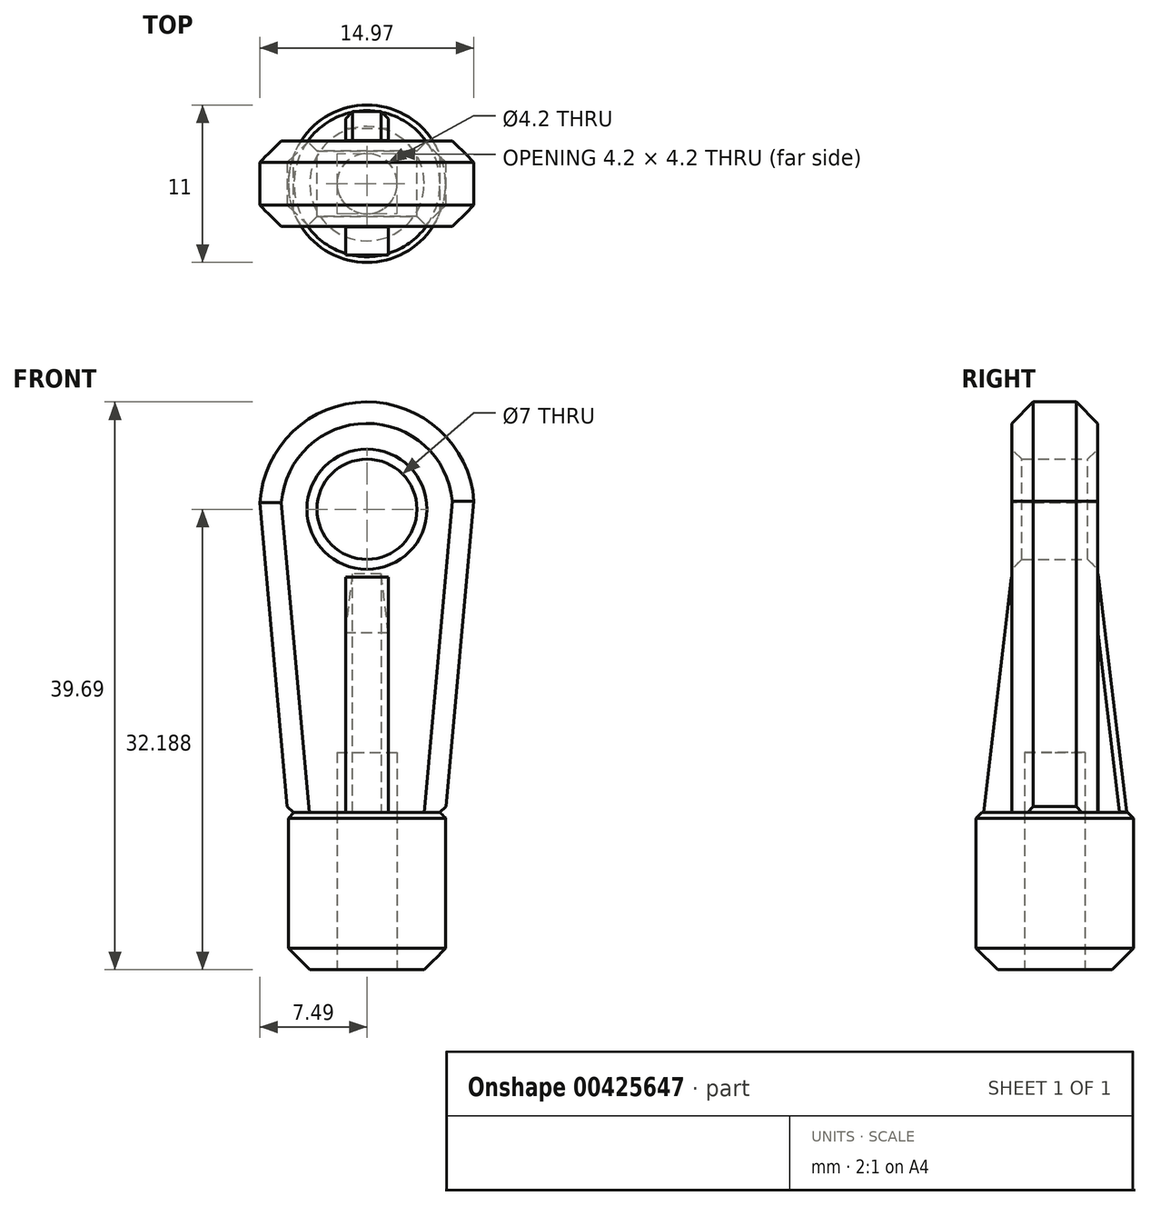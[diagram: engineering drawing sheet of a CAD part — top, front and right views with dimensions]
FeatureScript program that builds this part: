
annotation { "Feature Type Name" : "Feature", "Feature Type Description" : "" }
export const myFeature = defineFeature(function(context is Context, id is Id, definition is map)
    precondition{}
    {
        {
            var Q0;
            Q0=qCreatedBy(makeId("Top.planeOp"),FACE);
            var sketch = newSketch(context, id + "F0", { "sketchPlane" : qUnion([Q0])});
            skCircle(sketch, "E0", {"center": v(0, 0) * mm, "radius": 5.5 * mm});
            skSolve(sketch);
        }
        {
            var Q0;
            Q0=makeQuery(id+"F0.imprint","IMPRINT",FACE,{"disambiguationData":[TD([[makeQuery(id+"F0.imprint","IMPRINT",EDGE,{"derivedFrom":sQuery(id+"F0.wireOp",EDGE,"E0")}),1.0]])]});
            extrude(context, id + "F1", {"entities" : qUnion([Q0]), "depth" : 11 * mm});
        }
        {
            var Q0;
            Q0=qCreatedBy(makeId("Front.planeOp"),FACE);
            var sketch = newSketch(context, id + "F2", { "sketchPlane" : qUnion([Q0])});
            skCircle(sketch, "E1", {"center": v(0, 32.19) * mm, "radius": 3.5 * mm});
            skCircle(sketch, "E2", {"center": v(0, 32.19) * mm, "radius": 7.5 * mm});
            skLineSegment(sketch, "E3", {"start": v(-7.49, 32.64) * mm, "end": v(-5.53, 11) * mm});
            skLineSegment(sketch, "E4", {"start": v(-5.53, 11) * mm, "end": v(5.5, 11) * mm});
            skLineSegment(sketch, "E5", {"start": v(5.5, 11) * mm, "end": v(7.48, 32.76) * mm});
            skSolve(sketch);
        }
        {
            var Q0;
            {var subQ5=sQuery(id+"F2.wireOp",EDGE,"E4");Q0=makeQuery(id+"F2.imprint","IMPRINT",FACE,{"disambiguationData":[TD([[makeQuery(id+"F2.imprint","IMPRINT",EDGE,{"derivedFrom":subQ5}),1.0]])]});}
            extrude(context, id + "F3", {"entities" : qUnion([Q0]), "depth" : 3 * mm, "hasSecondDirection" : true, "secondDirectionOppositeDirection" : true, "secondDirectionDepth" : 3 * mm});
        }
        {
            var Q0;
            Q0=makeQuery(id+"F2.imprint","IMPRINT",FACE,{"disambiguationData":[TD([[makeQuery(id+"F2.imprint","IMPRINT",EDGE,{"derivedFrom":sQuery(id+"F2.wireOp",EDGE,"E1")}),-1.0]])]});
            extrude(context, id + "F4", {"entities" : qUnion([Q0]), "operationType" : NewBodyOperationType.ADD, "depth" : 3 * mm, "hasSecondDirection" : true, "secondDirectionOppositeDirection" : true, "secondDirectionDepth" : 3 * mm});
        }
        {
            var Q0;
            {var subQ0=sQuery(id+"F2.wireOp",EDGE,"E2");Q0=makeQuery(id+"F4.opExtrude","CAP_EDGE",EDGE,{"disambiguationData":[OSD([subQ0]),TDD([makeQuery(id+"F2.imprint","IMPRINT",EDGE,{"disambiguationData":[TD([[makeQuery(id+"F2.imprint","INTERSECT",VERTEX,{"disambiguationData":[OD(0.0)],"derivedFrom":[subQ0,sQuery(id+"F2.wireOp",EDGE,"E3")]}),1.0]])],"derivedFrom":subQ0})])],"isStart":false});}
            var Q1;
            {var subQ0=sQuery(id+"F2.wireOp",EDGE,"E5");Q1=makeQuery(id+"F4.boolean.opBoolean","MERGE",EDGE,{"derivedFrom":[makeQuery(id+"F3.opExtrude","CAP_EDGE",EDGE,{"disambiguationData":[OSD([subQ0])],"isStart":false}),makeQuery(id+"F4.opExtrude","CAP_EDGE",EDGE,{"disambiguationData":[OSD([subQ0])],"isStart":false})]});}
            var Q2;
            {var subQ0=sQuery(id+"F2.wireOp",EDGE,"E3");Q2=makeQuery(id+"F4.boolean.opBoolean","MERGE",EDGE,{"derivedFrom":[makeQuery(id+"F3.opExtrude","CAP_EDGE",EDGE,{"disambiguationData":[OSD([subQ0])],"isStart":false}),makeQuery(id+"F4.opExtrude","CAP_EDGE",EDGE,{"disambiguationData":[OSD([subQ0])],"isStart":false})]});}
            chamfer(context, id + "F5", {"entities" : qUnion([Q0, Q1, Q2]), "width" : 1.5 * mm, "tangentPropagation" : true});
        }
        {
            var Q0;
            {var subQ0=sQuery(id+"F2.wireOp",EDGE,"E3");Q0=makeQuery(id+"F4.boolean.opBoolean","MERGE",EDGE,{"derivedFrom":[makeQuery(id+"F3.opExtrude","CAP_EDGE",EDGE,{"disambiguationData":[OSD([subQ0])],"isStart":true}),makeQuery(id+"F4.opExtrude","CAP_EDGE",EDGE,{"disambiguationData":[OSD([subQ0])],"isStart":true})]});}
            var Q1;
            {var subQ0=sQuery(id+"F2.wireOp",EDGE,"E2");Q1=makeQuery(id+"F4.opExtrude","CAP_EDGE",EDGE,{"disambiguationData":[OSD([subQ0]),TDD([makeQuery(id+"F2.imprint","IMPRINT",EDGE,{"disambiguationData":[TD([[makeQuery(id+"F2.imprint","INTERSECT",VERTEX,{"disambiguationData":[OD(0.0)],"derivedFrom":[subQ0,sQuery(id+"F2.wireOp",EDGE,"E3")]}),1.0]])],"derivedFrom":subQ0})])],"isStart":true});}
            var Q2;
            {var subQ0=sQuery(id+"F2.wireOp",EDGE,"E5");Q2=makeQuery(id+"F4.boolean.opBoolean","MERGE",EDGE,{"derivedFrom":[makeQuery(id+"F3.opExtrude","CAP_EDGE",EDGE,{"disambiguationData":[OSD([subQ0])],"isStart":true}),makeQuery(id+"F4.opExtrude","CAP_EDGE",EDGE,{"disambiguationData":[OSD([subQ0])],"isStart":true})]});}
            chamfer(context, id + "F6", {"entities" : qUnion([Q0, Q1, Q2]), "width" : 1.5 * mm, "tangentPropagation" : true});
        }
        {
            var Q0;
            Q0=makeQuery(id+"F4.opExtrude","CAP_EDGE",EDGE,{"disambiguationData":[OSD([sQuery(id+"F2.wireOp",EDGE,"E1")])],"isStart":false});
            chamfer(context, id + "F7", {"entities" : qUnion([Q0]), "width" : 0.7 * mm, "tangentPropagation" : true});
        }
        {
            var Q0;
            Q0=makeQuery(id+"F4.opExtrude","CAP_EDGE",EDGE,{"disambiguationData":[OSD([sQuery(id+"F2.wireOp",EDGE,"E1")])],"isStart":true});
            chamfer(context, id + "F8", {"entities" : qUnion([Q0]), "width" : 0.7 * mm, "tangentPropagation" : true});
        }
        {
            var Q0;
            Q0=makeQuery(id+"F1.opExtrude","CAP_EDGE",EDGE,{"disambiguationData":[OSD([sQuery(id+"F0.wireOp",EDGE,"E0")])],"isStart":false});
            chamfer(context, id + "F9", {"entities" : qUnion([Q0]), "width" : 0.4 * mm, "tangentPropagation" : true});
        }
        {
            var Q0;
            Q0=makeQuery(id+"F3.opExtrude","SWEPT_EDGE",EDGE,{"disambiguationData":[OSD([sQuery(id+"F2.wireOp",EDGE,"E3"),sQuery(id+"F2.wireOp",EDGE,"E4")])]});
            chamfer(context, id + "F10", {"entities" : qUnion([Q0]), "width" : 0.4 * mm, "tangentPropagation" : true});
        }
        {
            var Q0;
            Q0=makeQuery(id+"F3.opExtrude","SWEPT_EDGE",EDGE,{"disambiguationData":[OSD([sQuery(id+"F2.wireOp",EDGE,"E4"),sQuery(id+"F2.wireOp",EDGE,"E5")])]});
            chamfer(context, id + "F11", {"entities" : qUnion([Q0]), "width" : 0.4 * mm, "tangentPropagation" : true});
        }
        {
            var Q0;
            Q0=qCreatedBy(makeId("Right.planeOp"),FACE);
            var sketch = newSketch(context, id + "F12", { "sketchPlane" : qUnion([Q0])});
            skLineSegment(sketch, "E6", {"start": v(5.03, 11.03) * mm, "end": v(3.02, 27.67) * mm});
            skLineSegment(sketch, "E7", {"start": v(3.02, 27.67) * mm, "end": v(3.02, 10.98) * mm});
            skLineSegment(sketch, "E8", {"start": v(3.02, 10.98) * mm, "end": v(5.03, 11.03) * mm});
            skSolve(sketch);
        }
        {
            var Q0;
            Q0 = qSketchRegion(id + "F12", true);
            extrude(context, id + "F13", {"entities" : qUnion([Q0]), "operationType" : NewBodyOperationType.ADD, "depth" : 1.5 * mm, "hasSecondDirection" : true, "secondDirectionOppositeDirection" : true, "secondDirectionDepth" : 1.5 * mm});
        }
        {
            var Q0;
            Q0=qCreatedBy(makeId("Right.planeOp"),FACE);
            var sketch = newSketch(context, id + "F14", { "sketchPlane" : qUnion([Q0])});
            skLineSegment(sketch, "E9", {"start": v(-2.93, 11) * mm, "end": v(-4.98, 11) * mm});
            skLineSegment(sketch, "E10", {"start": v(-4.98, 11) * mm, "end": v(-3.02, 27.44) * mm});
            skLineSegment(sketch, "E11", {"start": v(-3.02, 27.44) * mm, "end": v(-2.93, 11) * mm});
            skSolve(sketch);
        }
        {
            var Q0;
            Q0 = qSketchRegion(id + "F14", true);
            extrude(context, id + "F15", {"entities" : qUnion([Q0]), "operationType" : NewBodyOperationType.ADD, "depth" : 1.5 * mm, "hasSecondDirection" : true, "secondDirectionOppositeDirection" : true, "secondDirectionDepth" : 1.5 * mm});
        }
        {
            var Q0;
            Q0=makeQuery(id+"F1.opExtrude","CAP_FACE",FACE,{"disambiguationData":[OSD([sQuery(id+"F0.wireOp",EDGE,"E0")])],"isStart":true});
            var sketch = newSketch(context, id + "F16", { "sketchPlane" : qUnion([Q0])});
            skCircle(sketch, "E12", {"center": v(0, 0) * mm, "radius": 2.1 * mm});
            skSolve(sketch);
        }
        {
            var Q0;
            Q0=makeQuery(id+"F16.imprint","IMPRINT",FACE,{"disambiguationData":[TD([[makeQuery(id+"F16.imprint","IMPRINT",EDGE,{"derivedFrom":sQuery(id+"F16.wireOp",EDGE,"E12")}),1.0]])]});
            extrude(context, id + "F17", {"entities" : qUnion([Q0]), "operationType" : NewBodyOperationType.REMOVE, "oppositeDirection" : true, "depth" : 15.2 * mm});
        }
        {
            var Q0;
            Q0=makeQuery(id+"F1.opExtrude","CAP_EDGE",EDGE,{"disambiguationData":[OSD([sQuery(id+"F0.wireOp",EDGE,"E0")])],"isStart":true});
            chamfer(context, id + "F18", {"entities" : qUnion([Q0]), "width" : 1.5 * mm, "tangentPropagation" : true});
        }
        {
            var Q0;
            Q0=makeQuery(id+"F13.opExtrude","CAP_EDGE",EDGE,{"disambiguationData":[OSD([sQuery(id+"F12.wireOp",EDGE,"E6")])],"isStart":false});
            var Q1;
            Q1=makeQuery(id+"F13.opExtrude","CAP_EDGE",EDGE,{"disambiguationData":[OSD([sQuery(id+"F12.wireOp",EDGE,"E6")])],"isStart":true});
            chamfer(context, id + "F19", {"entities" : qUnion([Q0, Q1]), "width" : 0.5 * mm});
        }
    });
